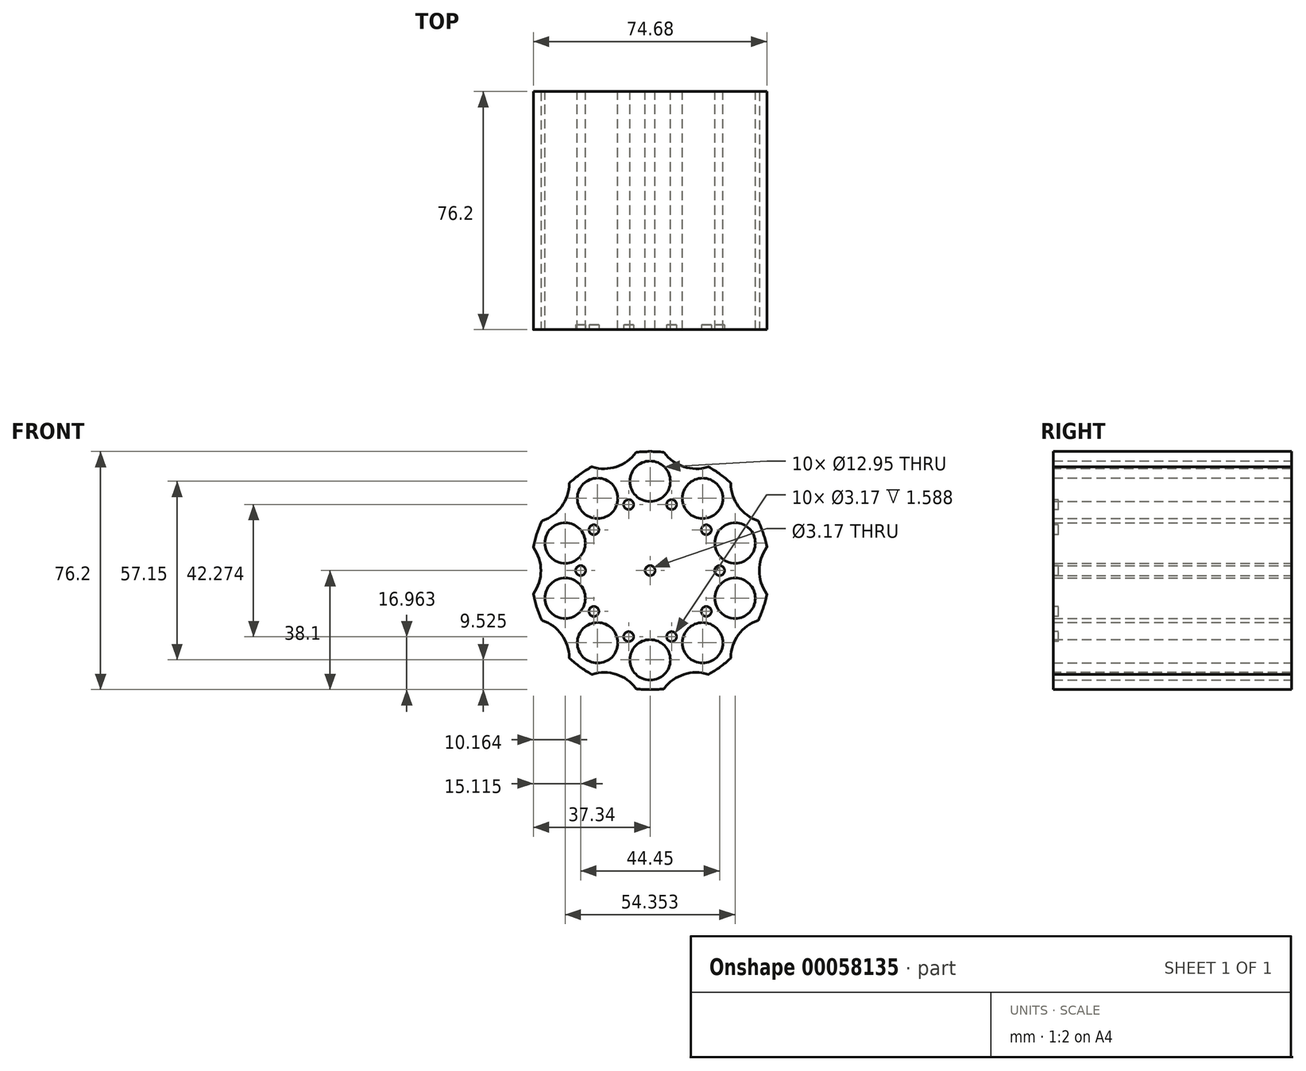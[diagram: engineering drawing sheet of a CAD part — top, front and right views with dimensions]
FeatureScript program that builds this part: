
annotation { "Feature Type Name" : "Feature", "Feature Type Description" : "" }
export const myFeature = defineFeature(function(context is Context, id is Id, definition is map)
    precondition{}
    {
        {
            var Q0;
            Q0=qCreatedBy(makeId("Front.planeOp"),FACE);
            var sketch = newSketch(context, id + "F0", { "sketchPlane" : qUnion([Q0])});
            skCircle(sketch, "E0", {"center": v(0, 0) * mm, "radius": 28.58 * mm, "construction": true});
            skCircle(sketch, "E1", {"center": v(0, 28.58) * mm, "radius": 6.48 * mm});
            skCircle(sketch, "E2.1.0", {"center": v(-16.8, 23.12) * mm, "radius": 6.48 * mm});
            skCircle(sketch, "E2.2.0", {"center": v(-27.18, 8.83) * mm, "radius": 6.48 * mm});
            skCircle(sketch, "E2.3.0", {"center": v(-27.18, -8.83) * mm, "radius": 6.48 * mm});
            skCircle(sketch, "E2.4.0", {"center": v(-16.8, -23.12) * mm, "radius": 6.48 * mm});
            skCircle(sketch, "E2.5.0", {"center": v(0, -28.58) * mm, "radius": 6.48 * mm});
            skCircle(sketch, "E2.6.0", {"center": v(16.8, -23.12) * mm, "radius": 6.48 * mm});
            skCircle(sketch, "E2.7.0", {"center": v(27.18, -8.83) * mm, "radius": 6.48 * mm});
            skCircle(sketch, "E2.8.0", {"center": v(27.18, 8.83) * mm, "radius": 6.48 * mm});
            skCircle(sketch, "E2.9.0", {"center": v(16.8, 23.12) * mm, "radius": 6.48 * mm});
            skCircle(sketch, "E3", {"center": v(0, 0) * mm, "radius": 38.1 * mm});
            skCircle(sketch, "E4", {"center": v(0, 0) * mm, "radius": 1.59 * mm});
            skCircle(sketch, "E5", {"center": v(0, 0) * mm, "radius": 19.05 * mm, "construction": true});
            skSolve(sketch);
        }
        {
            var Q0;
            Q0 = qSketchRegion(id + "F0", true);
            extrude(context, id + "F1", {"entities" : qUnion([Q0]), "depth" : 76.2 * mm});
        }
        {
            var Q0;
            Q0=makeQuery(id+"F1.opExtrude","CAP_FACE",FACE,{"disambiguationData":[OSD([sQuery(id+"F0.wireOp",EDGE,"E1"),sQuery(id+"F0.wireOp",EDGE,"E2.1.0"),sQuery(id+"F0.wireOp",EDGE,"E2.2.0"),sQuery(id+"F0.wireOp",EDGE,"E2.3.0"),sQuery(id+"F0.wireOp",EDGE,"E2.4.0"),sQuery(id+"F0.wireOp",EDGE,"E2.5.0"),sQuery(id+"F0.wireOp",EDGE,"E2.6.0"),sQuery(id+"F0.wireOp",EDGE,"E2.7.0"),sQuery(id+"F0.wireOp",EDGE,"E2.8.0"),sQuery(id+"F0.wireOp",EDGE,"E2.9.0"),sQuery(id+"F0.wireOp",EDGE,"E3"),sQuery(id+"F0.wireOp",EDGE,"E4")])],"isStart":false});
            var sketch = newSketch(context, id + "F2", { "sketchPlane" : qUnion([Q0])});
            skCircle(sketch, "E6", {"center": v(0, 0) * mm, "radius": 22.23 * mm, "construction": true});
            skCircle(sketch, "E7", {"center": v(6.87, 21.14) * mm, "radius": 1.59 * mm});
            skCircle(sketch, "E8.1.1", {"center": v(-6.87, 21.14) * mm, "radius": 1.59 * mm});
            skCircle(sketch, "E8.2.1", {"center": v(-17.98, 13.06) * mm, "radius": 1.59 * mm});
            skCircle(sketch, "E8.3.1", {"center": v(-22.23, 0) * mm, "radius": 1.59 * mm});
            skCircle(sketch, "E8.4.1", {"center": v(-17.98, -13.06) * mm, "radius": 1.59 * mm});
            skCircle(sketch, "E8.5.1", {"center": v(-6.87, -21.14) * mm, "radius": 1.59 * mm});
            skCircle(sketch, "E8.6.1", {"center": v(6.87, -21.14) * mm, "radius": 1.59 * mm});
            skCircle(sketch, "E8.7.1", {"center": v(17.98, -13.06) * mm, "radius": 1.59 * mm});
            skCircle(sketch, "E8.8.1", {"center": v(22.23, 0) * mm, "radius": 1.59 * mm});
            skCircle(sketch, "E8.9.1", {"center": v(17.98, 13.06) * mm, "radius": 1.59 * mm});
            skLineSegment(sketch, "E9", {"start": v(0, 0) * mm, "end": v(-18.79, 57.82) * mm, "construction": true});
            skSolve(sketch);
        }
        {
            var Q0;
            Q0 = qSketchRegion(id + "F2", true);
            extrude(context, id + "F3", {"entities" : qUnion([Q0]), "operationType" : NewBodyOperationType.REMOVE, "oppositeDirection" : true, "depth" : 1.59 * mm});
        }
        {
            var Q0;
            Q0=makeQuery(id+"F1.opExtrude","CAP_FACE",FACE,{"disambiguationData":[OSD([sQuery(id+"F0.wireOp",EDGE,"E1"),sQuery(id+"F0.wireOp",EDGE,"E2.1.0"),sQuery(id+"F0.wireOp",EDGE,"E2.2.0"),sQuery(id+"F0.wireOp",EDGE,"E2.3.0"),sQuery(id+"F0.wireOp",EDGE,"E2.4.0"),sQuery(id+"F0.wireOp",EDGE,"E2.5.0"),sQuery(id+"F0.wireOp",EDGE,"E2.6.0"),sQuery(id+"F0.wireOp",EDGE,"E2.7.0"),sQuery(id+"F0.wireOp",EDGE,"E2.8.0"),sQuery(id+"F0.wireOp",EDGE,"E2.9.0"),sQuery(id+"F0.wireOp",EDGE,"E3"),sQuery(id+"F0.wireOp",EDGE,"E4")])],"isStart":false});
            var sketch = newSketch(context, id + "F4", { "sketchPlane" : qUnion([Q0])});
            skLineSegment(sketch, "E10", {"start": v(0, 0) * mm, "end": v(14.72, 45.3) * mm, "construction": true});
            skCircle(sketch, "E11", {"center": v(14.72, 45.3) * mm, "radius": 12.7 * mm});
            skPoint(sketch, "E12", {"position": v(4.43, 37.84) * mm});
            skPoint(sketch, "E13", {"position": v(18.66, 33.22) * mm});
            skCircle(sketch, "E14.1.0", {"center": v(-14.72, 45.3) * mm, "radius": 12.7 * mm});
            skCircle(sketch, "E14.2.0", {"center": v(-38.53, 28) * mm, "radius": 12.7 * mm});
            skCircle(sketch, "E14.3.0", {"center": v(-47.63, 0) * mm, "radius": 12.7 * mm});
            skCircle(sketch, "E14.4.0", {"center": v(-38.53, -28) * mm, "radius": 12.7 * mm});
            skCircle(sketch, "E14.5.0", {"center": v(-14.72, -45.3) * mm, "radius": 12.7 * mm});
            skCircle(sketch, "E14.6.0", {"center": v(14.72, -45.3) * mm, "radius": 12.7 * mm});
            skCircle(sketch, "E14.7.0", {"center": v(38.53, -28) * mm, "radius": 12.7 * mm});
            skCircle(sketch, "E14.8.0", {"center": v(47.62, 0) * mm, "radius": 12.7 * mm});
            skCircle(sketch, "E14.9.0", {"center": v(38.53, 28) * mm, "radius": 12.7 * mm});
            skPoint(sketch, "E14.center", {"position": v(0, 0) * mm});
            skSolve(sketch);
        }
        {
            var Q0;
            Q0 = qSketchRegion(id + "F4", true);
            extrude(context, id + "F5", {"entities" : qUnion([Q0]), "operationType" : NewBodyOperationType.REMOVE, "endBound" : BoundingType.THROUGH_ALL, "oppositeDirection" : true, "depth" : 25.4 * mm});
        }
        {
            var Q0;
            Q0=makeQuery(id+"F5.boolean.opBoolean","INTERSECT",EDGE,{"disambiguationData":[OD(0.0)],"derivedFrom":[makeQuery(id+"F1.opExtrude","SWEPT_FACE",FACE,{"disambiguationData":[OSD([sQuery(id+"F0.wireOp",EDGE,"E3")])]}),makeQuery(id+"F5.opExtrude","SWEPT_FACE",FACE,{"disambiguationData":[OSD([sQuery(id+"F4.wireOp",EDGE,"E14.2.0")])]})]});
            var Q1;
            Q1=makeQuery(id+"F5.boolean.opBoolean","INTERSECT",EDGE,{"disambiguationData":[OD(1.0)],"derivedFrom":[makeQuery(id+"F1.opExtrude","SWEPT_FACE",FACE,{"disambiguationData":[OSD([sQuery(id+"F0.wireOp",EDGE,"E3")])]}),makeQuery(id+"F5.opExtrude","SWEPT_FACE",FACE,{"disambiguationData":[OSD([sQuery(id+"F4.wireOp",EDGE,"E14.2.0")])]})]});
            var Q2;
            Q2=makeQuery(id+"F5.boolean.opBoolean","INTERSECT",EDGE,{"disambiguationData":[OD(0.0)],"derivedFrom":[makeQuery(id+"F1.opExtrude","SWEPT_FACE",FACE,{"disambiguationData":[OSD([sQuery(id+"F0.wireOp",EDGE,"E3")])]}),makeQuery(id+"F5.opExtrude","SWEPT_FACE",FACE,{"disambiguationData":[OSD([sQuery(id+"F4.wireOp",EDGE,"E14.3.0")])]})]});
            var Q3;
            Q3=makeQuery(id+"F5.boolean.opBoolean","INTERSECT",EDGE,{"disambiguationData":[OD(1.0)],"derivedFrom":[makeQuery(id+"F1.opExtrude","SWEPT_FACE",FACE,{"disambiguationData":[OSD([sQuery(id+"F0.wireOp",EDGE,"E3")])]}),makeQuery(id+"F5.opExtrude","SWEPT_FACE",FACE,{"disambiguationData":[OSD([sQuery(id+"F4.wireOp",EDGE,"E14.3.0")])]})]});
            var Q4;
            Q4=makeQuery(id+"F5.boolean.opBoolean","INTERSECT",EDGE,{"disambiguationData":[OD(0.0)],"derivedFrom":[makeQuery(id+"F1.opExtrude","SWEPT_FACE",FACE,{"disambiguationData":[OSD([sQuery(id+"F0.wireOp",EDGE,"E3")])]}),makeQuery(id+"F5.opExtrude","SWEPT_FACE",FACE,{"disambiguationData":[OSD([sQuery(id+"F4.wireOp",EDGE,"E14.4.0")])]})]});
            var Q5;
            Q5=makeQuery(id+"F5.boolean.opBoolean","INTERSECT",EDGE,{"disambiguationData":[OD(1.0)],"derivedFrom":[makeQuery(id+"F1.opExtrude","SWEPT_FACE",FACE,{"disambiguationData":[OSD([sQuery(id+"F0.wireOp",EDGE,"E3")])]}),makeQuery(id+"F5.opExtrude","SWEPT_FACE",FACE,{"disambiguationData":[OSD([sQuery(id+"F4.wireOp",EDGE,"E14.4.0")])]})]});
            var Q6;
            Q6=makeQuery(id+"F5.boolean.opBoolean","INTERSECT",EDGE,{"disambiguationData":[OD(0.0)],"derivedFrom":[makeQuery(id+"F1.opExtrude","SWEPT_FACE",FACE,{"disambiguationData":[OSD([sQuery(id+"F0.wireOp",EDGE,"E3")])]}),makeQuery(id+"F5.opExtrude","SWEPT_FACE",FACE,{"disambiguationData":[OSD([sQuery(id+"F4.wireOp",EDGE,"E14.5.0")])]})]});
            var Q7;
            Q7=makeQuery(id+"F5.boolean.opBoolean","INTERSECT",EDGE,{"disambiguationData":[OD(1.0)],"derivedFrom":[makeQuery(id+"F1.opExtrude","SWEPT_FACE",FACE,{"disambiguationData":[OSD([sQuery(id+"F0.wireOp",EDGE,"E3")])]}),makeQuery(id+"F5.opExtrude","SWEPT_FACE",FACE,{"disambiguationData":[OSD([sQuery(id+"F4.wireOp",EDGE,"E14.5.0")])]})]});
            var Q8;
            Q8=makeQuery(id+"F5.boolean.opBoolean","INTERSECT",EDGE,{"disambiguationData":[OD(0.0)],"derivedFrom":[makeQuery(id+"F1.opExtrude","SWEPT_FACE",FACE,{"disambiguationData":[OSD([sQuery(id+"F0.wireOp",EDGE,"E3")])]}),makeQuery(id+"F5.opExtrude","SWEPT_FACE",FACE,{"disambiguationData":[OSD([sQuery(id+"F4.wireOp",EDGE,"E14.6.0")])]})]});
            var Q9;
            Q9=makeQuery(id+"F5.boolean.opBoolean","INTERSECT",EDGE,{"disambiguationData":[OD(1.0)],"derivedFrom":[makeQuery(id+"F1.opExtrude","SWEPT_FACE",FACE,{"disambiguationData":[OSD([sQuery(id+"F0.wireOp",EDGE,"E3")])]}),makeQuery(id+"F5.opExtrude","SWEPT_FACE",FACE,{"disambiguationData":[OSD([sQuery(id+"F4.wireOp",EDGE,"E14.6.0")])]})]});
            var Q10;
            Q10=makeQuery(id+"F5.boolean.opBoolean","INTERSECT",EDGE,{"disambiguationData":[OD(1.0)],"derivedFrom":[makeQuery(id+"F1.opExtrude","SWEPT_FACE",FACE,{"disambiguationData":[OSD([sQuery(id+"F0.wireOp",EDGE,"E3")])]}),makeQuery(id+"F5.opExtrude","SWEPT_FACE",FACE,{"disambiguationData":[OSD([sQuery(id+"F4.wireOp",EDGE,"E14.7.0")])]})]});
            var Q11;
            Q11=makeQuery(id+"F5.boolean.opBoolean","INTERSECT",EDGE,{"disambiguationData":[OD(0.0)],"derivedFrom":[makeQuery(id+"F1.opExtrude","SWEPT_FACE",FACE,{"disambiguationData":[OSD([sQuery(id+"F0.wireOp",EDGE,"E3")])]}),makeQuery(id+"F5.opExtrude","SWEPT_FACE",FACE,{"disambiguationData":[OSD([sQuery(id+"F4.wireOp",EDGE,"E14.8.0")])]})]});
            var Q12;
            Q12=makeQuery(id+"F5.boolean.opBoolean","INTERSECT",EDGE,{"disambiguationData":[OD(1.0)],"derivedFrom":[makeQuery(id+"F1.opExtrude","SWEPT_FACE",FACE,{"disambiguationData":[OSD([sQuery(id+"F0.wireOp",EDGE,"E3")])]}),makeQuery(id+"F5.opExtrude","SWEPT_FACE",FACE,{"disambiguationData":[OSD([sQuery(id+"F4.wireOp",EDGE,"E14.9.0")])]})]});
            var Q13;
            Q13=makeQuery(id+"F5.boolean.opBoolean","INTERSECT",EDGE,{"disambiguationData":[OD(1.0)],"derivedFrom":[makeQuery(id+"F1.opExtrude","SWEPT_FACE",FACE,{"disambiguationData":[OSD([sQuery(id+"F0.wireOp",EDGE,"E3")])]}),makeQuery(id+"F5.opExtrude","SWEPT_FACE",FACE,{"disambiguationData":[OSD([sQuery(id+"F4.wireOp",EDGE,"E14.8.0")])]})]});
            var Q14;
            Q14=makeQuery(id+"F5.boolean.opBoolean","INTERSECT",EDGE,{"disambiguationData":[OD(0.0)],"derivedFrom":[makeQuery(id+"F1.opExtrude","SWEPT_FACE",FACE,{"disambiguationData":[OSD([sQuery(id+"F0.wireOp",EDGE,"E3")])]}),makeQuery(id+"F5.opExtrude","SWEPT_FACE",FACE,{"disambiguationData":[OSD([sQuery(id+"F4.wireOp",EDGE,"E14.9.0")])]})]});
            var Q15;
            Q15=makeQuery(id+"F5.boolean.opBoolean","INTERSECT",EDGE,{"disambiguationData":[OD(1.0)],"derivedFrom":[makeQuery(id+"F1.opExtrude","SWEPT_FACE",FACE,{"disambiguationData":[OSD([sQuery(id+"F0.wireOp",EDGE,"E3")])]}),makeQuery(id+"F5.opExtrude","SWEPT_FACE",FACE,{"disambiguationData":[OSD([sQuery(id+"F4.wireOp",EDGE,"E11")])]})]});
            var Q16;
            Q16=makeQuery(id+"F5.boolean.opBoolean","INTERSECT",EDGE,{"disambiguationData":[OD(1.0)],"derivedFrom":[makeQuery(id+"F1.opExtrude","SWEPT_FACE",FACE,{"disambiguationData":[OSD([sQuery(id+"F0.wireOp",EDGE,"E3")])]}),makeQuery(id+"F5.opExtrude","SWEPT_FACE",FACE,{"disambiguationData":[OSD([sQuery(id+"F4.wireOp",EDGE,"E14.1.0")])]})]});
            var Q17;
            Q17=makeQuery(id+"F5.boolean.opBoolean","INTERSECT",EDGE,{"disambiguationData":[OD(0.0)],"derivedFrom":[makeQuery(id+"F1.opExtrude","SWEPT_FACE",FACE,{"disambiguationData":[OSD([sQuery(id+"F0.wireOp",EDGE,"E3")])]}),makeQuery(id+"F5.opExtrude","SWEPT_FACE",FACE,{"disambiguationData":[OSD([sQuery(id+"F4.wireOp",EDGE,"E14.1.0")])]})]});
            var Q18;
            Q18=makeQuery(id+"F5.boolean.opBoolean","INTERSECT",EDGE,{"disambiguationData":[OD(0.0)],"derivedFrom":[makeQuery(id+"F1.opExtrude","SWEPT_FACE",FACE,{"disambiguationData":[OSD([sQuery(id+"F0.wireOp",EDGE,"E3")])]}),makeQuery(id+"F5.opExtrude","SWEPT_FACE",FACE,{"disambiguationData":[OSD([sQuery(id+"F4.wireOp",EDGE,"E11")])]})]});
            var Q19;
            Q19=makeQuery(id+"F5.boolean.opBoolean","INTERSECT",EDGE,{"disambiguationData":[OD(0.0)],"derivedFrom":[makeQuery(id+"F1.opExtrude","SWEPT_FACE",FACE,{"disambiguationData":[OSD([sQuery(id+"F0.wireOp",EDGE,"E3")])]}),makeQuery(id+"F5.opExtrude","SWEPT_FACE",FACE,{"disambiguationData":[OSD([sQuery(id+"F4.wireOp",EDGE,"E14.7.0")])]})]});
            fillet(context, id + "F6", {"entities" : qUnion([Q0, Q1, Q2, Q3, Q4, Q5, Q6, Q7, Q8, Q9, Q10, Q11, Q12, Q13, Q14, Q15, Q16, Q17, Q18, Q19]), "radius" : 0.25 * mm, "tangentPropagation" : true, "allowEdgeOverflow" : false});
        }
    });
